# Revit family: Tap-Single deck_mounted-PRESTO-NEO S CHAUD 7SEC-65305
name_source: partatom
category: Plumbing Fixtures
revit_build: Autodesk Revit 2014 (Build: 20130308_1515(x64)
units: mm (PartAtom-declared; Revit-internal decimal feet)

## types (1)
- 65305
    CW Inlet = 0 mm  [stored 0 ft]
    Default Elevation = 1219 mm
    Description = PRESTO NEO S Single deck-mounted tap
    Drain Connection = 0 mm  [stored 0 ft]
    Edition number = 1
    Flow (at 3 bar - 4-position flow adjustment device) = 0.1 L/s
    HW Inlet = 13 mm
    Height = 134 mm
    Manufacturer = PRESTO LES ROBINETS
    Manufacturer name = Presto
    Material main = Stainless steel
    Material secondary = Stainless steel
    Model = 65305
    Nominal height = 13400
    Nominal width = 12000
    Operating Pressure = 1 to 5 bar
    Outlet = 0 mm  [stored 0 ft]
    Primary Material = Stainless Steel-Presto
    Product Guid = bfd4fb46-1046-4cd8-a619-7da7ddcc43cb
    Product SKU = 65010
    Product data url = http://bimobject.com
    Product family = NEO
    Product group = ROBINET
    QR code = http://bimobject.com
    Temp - Resistance(30 minute Thermal Shock) = 75 °C
    Time flow (4 position adjustment) = 7 (± 5 sec.)
    Warranty = 10
    Weight Net (Kg) = 0
    Width = 120 mm  [stored 0.393701 ft]

note: [stored X ft] marks values corroborated as IEEE doubles in the binary element streams (Revit-internal decimal feet)

## geometry (parser evidence)
native form markers: Blend x2, Sweep x17
no freeform markers — native parametric forms only
